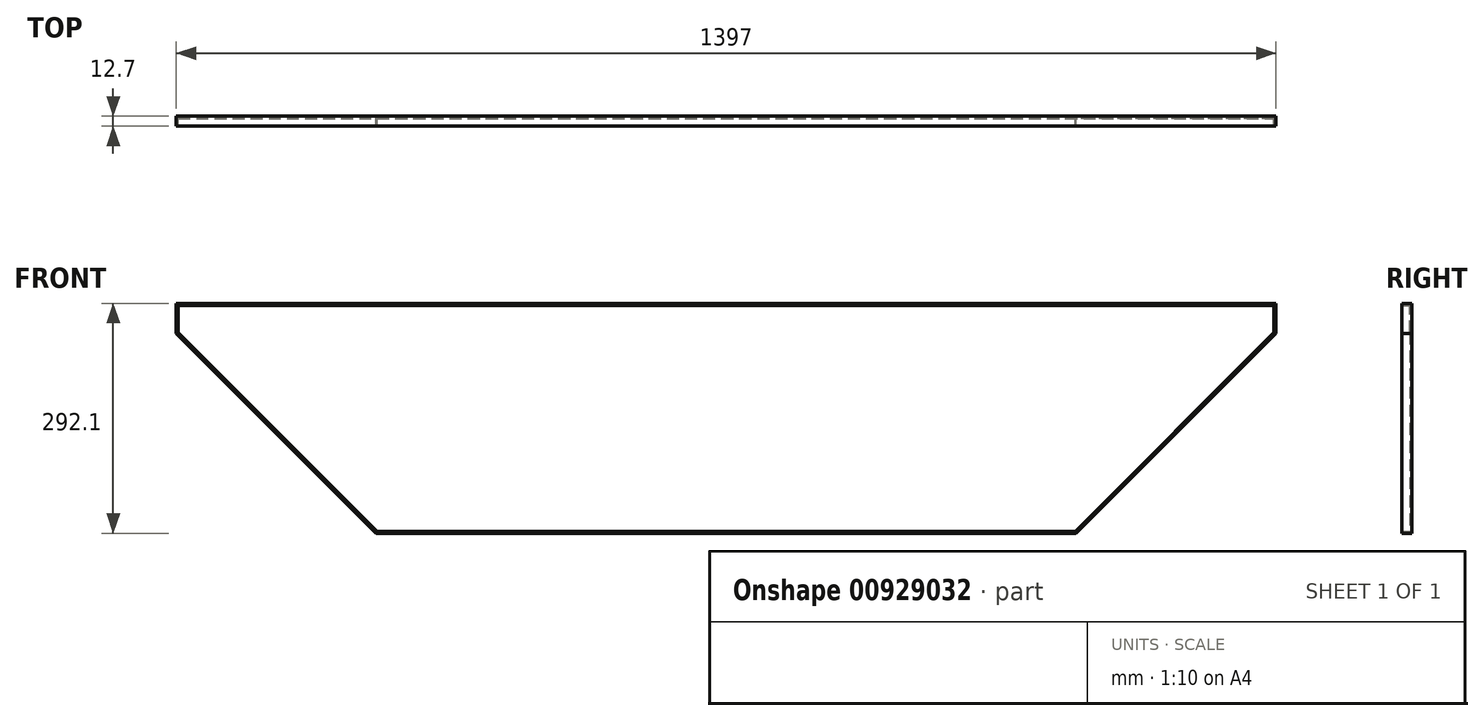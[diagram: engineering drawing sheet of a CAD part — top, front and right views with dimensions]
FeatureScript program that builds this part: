
annotation { "Feature Type Name" : "Feature", "Feature Type Description" : "" }
export const myFeature = defineFeature(function(context is Context, id is Id, definition is map)
    precondition{}
    {
        {
            var Q0;
            Q0=qCreatedBy(makeId("Front.planeOp"),FACE);
            var sketch = newSketch(context, id + "F0", { "sketchPlane" : qUnion([Q0])});
            skLineSegment(sketch, "E0.bottom", {"start": v(-444.5, 0) * mm, "end": v(444.5, 0) * mm});
            skLineSegment(sketch, "E0.top", {"start": v(-698.5, 292.1) * mm, "end": v(698.5, 292.1) * mm});
            skLineSegment(sketch, "E0.left", {"start": v(-698.5, 254) * mm, "end": v(-698.5, 292.1) * mm});
            skLineSegment(sketch, "E0.right", {"start": v(698.5, 254) * mm, "end": v(698.5, 292.1) * mm});
            skLineSegment(sketch, "E1", {"start": v(-698.5, 254) * mm, "end": v(-444.5, 0) * mm});
            skPoint(sketch, "E2.orphan", {"position": v(-698.5, 0) * mm});
            skLineSegment(sketch, "E3.MirrorCS", {"start": v(698.5, 254) * mm, "end": v(444.5, 0) * mm});
            skSolve(sketch);
        }
        {
            var Q0;
            Q0=makeQuery(id+"F0.imprint","IMPRINT",FACE,{"disambiguationData":[TD([[makeQuery(id+"F0.imprint","IMPRINT",EDGE,{"derivedFrom":sQuery(id+"F0.wireOp",EDGE,"E0.bottom")}),1.0]])]});
            extrude(context, id + "F1", {"entities" : qUnion([Q0]), "depth" : 12.7 * mm, "offsetDistance" : 25.4 * mm});
        }
        {
            var Q0;
            Q0=makeQuery(id+"F1.opExtrude","CAP_FACE",FACE,{"disambiguationData":[OSD([sQuery(id+"F0.wireOp",EDGE,"E0.bottom"),sQuery(id+"F0.wireOp",EDGE,"E0.top"),sQuery(id+"F0.wireOp",EDGE,"E0.left"),sQuery(id+"F0.wireOp",EDGE,"E0.right"),sQuery(id+"F0.wireOp",EDGE,"E1"),sQuery(id+"F0.wireOp",EDGE,"E3.MirrorCS")])],"isStart":false});
            shell(context, id + "F2", {"entities" : qUnion([Q0]), "thickness" : 2.67 * mm});
        }
    });
